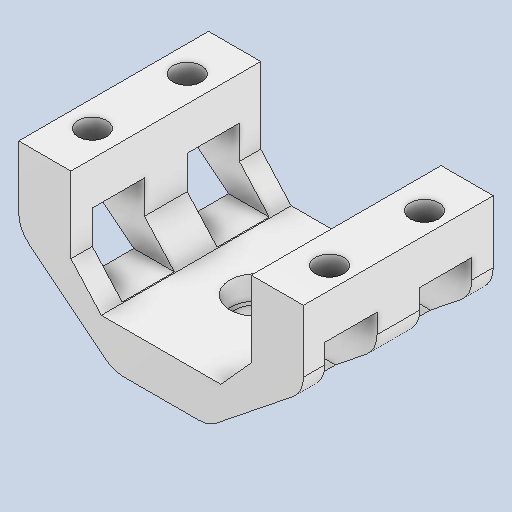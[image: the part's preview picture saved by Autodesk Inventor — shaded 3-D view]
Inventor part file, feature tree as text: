
AUTODESK INVENTOR PART (.ipt)
format: ipt  version: 2024.2 (Build 282272000, 272)  size: 317,440 bytes
history: native  units: in
note: dims shown in document units (in); Inventor stores cm internally (conversion verified against a paired STEP export)
features: extrude x2, sketch x2, other x1
ambient origin geometry x8: Origin, YZ Plane, XZ Plane, XY Plane, X Axis, Y Axis, Z Axis, Center Point
bodies: Solid1 (feature_tree)
feature tree (5):
  extrude  "Extrusion1"  Depth=0.7874in TaperAngle=0.0deg
  extrude  "Extrusion2"  Depth=0.1772in TaperAngle=0.0deg
  sketch  "Sketch1"  dims[d0=0.7874in d2=0.3937in d3=0.7874in d5=0.9843in d8=0.0394in d9=0.0in]
  sketch  "Sketch2"  dims[d10=0.1772in d11=0.1378in d12=0.0in]
  other  "Cortar-Extruir6"
